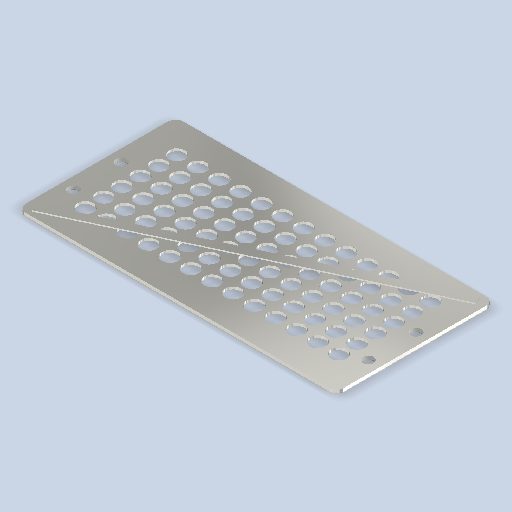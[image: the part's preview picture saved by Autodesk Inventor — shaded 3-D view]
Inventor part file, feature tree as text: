
AUTODESK INVENTOR PART (.ipt)
format: ipt  version: 2024 (Build 280153000, 153)  size: 349,696 bytes
history: native  units: mm
features: sketch x5, extrude x4, pattern_linear x2, fillet x1, hole x1
ambient origin geometry x8: Origin, YZ Plane, XZ Plane, XY Plane, X Axis, Y Axis, Z Axis, Center Point
bodies: Volumenkörper1 (feature_tree)
feature tree (13):
  extrude  "Extrusion1"  Depth=198.0mm
  extrude  "Extrusion2"  Depth=30.0mm
  extrude  "Extrusion3"  Depth=1.5mm TaperAngle=0.0deg
  pattern_linear  "Rechteckige Anordnung1"  Count1=2  [1 undecoded]
  pattern_linear  "Rechteckige Anordnung2"  Count1=6 Spacing1=23.0mm
  fillet  "Rundung1"  Radius=130.0mm
  hole  "Bohrung1"  [1 undecoded]
  extrude  "Extrusion5"  Depth=1.5mm
  sketch  "Skizze1"  dims[d0=400.0mm d1=198.0mm]
  sketch  "Skizze2"  dims[d2=4.5mm d3=0.0mm d4=30.0mm]
  sketch  "Skizze3"  dims[d5=30.0mm d6=1.5mm d7=0.0mm d8=20.0mm]
  sketch  "Skizze4"  dims[d9=1.5mm d10=0.0mm d11=60.0mm d13=23.0mm d14=130.0mm d16=26.5mm]
  sketch  "Skizze6"  dims[d17=10.0mm d18=13.376202mm d19=30.0mm d20=8.0mm d21=4.0mm d22=90.0deg d23=8.0mm d24=0.0mm d25=60.0mm d26=60.0mm d27=15.0mm d28=15.0mm d29=55.0mm d33=10.0mm d34=10.0mm d35=419.623641mm d36=1.5mm d37=0.0mm]
note: 2 required parameter values undecoded (feature->parameter linkage not recoverable at this tier; creation-order binding heuristic only, values carry confidence <= 0.55)
